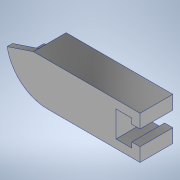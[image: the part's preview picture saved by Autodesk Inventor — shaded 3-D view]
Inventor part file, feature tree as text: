
AUTODESK INVENTOR PART (.ipt)
format: ipt  version: 2022 (Build 260153000, 153)  size: 173,568 bytes
history: native  units: mm
features: extrude x4, sketch x4, fillet x1
ambient origin geometry x8: Origin, YZ Plane, XZ Plane, XY Plane, X Axis, Y Axis, Z Axis, Center Point
bodies: Body1 (feature_tree), Body2 (feature_tree)
feature tree (9):
  extrude  "Extrusion2"  Depth=5.8mm
  extrude  "Extrusion7"  Depth=12.0mm TaperAngle=0.0deg
  extrude  "Extrusion10"  Depth=15.6mm
  fillet  "Fillet2"  [1 undecoded]
  extrude  "Extrusion11"  Depth=5.6mm
  sketch  "Sketch5"  dims[d41=5.8mm d48=44.0mm]
  sketch  "Sketch11"  dims[d50=3.0mm d56=12.0mm d57=0.0mm]
  sketch  "Sketch14"  dims[d63=45.0mm d67=15.6mm d71=0.0mm]
  sketch  "Sketch15"  dims[d72=36.2mm d87=5.6mm d88=9.5mm d95=17.453293mm d96=6.0mm d97=15.0mm d98=10.0mm d99=0.0mm d108=0.0mm d109=0.0mm d110=15.0mm d111=10.0mm d112=10.0mm d113=0.0mm d114=0.0mm d115=0.0mm]
note: 1 required parameter value undecoded (feature->parameter linkage not recoverable at this tier; creation-order binding heuristic only, values carry confidence <= 0.55)
